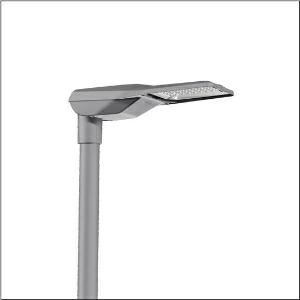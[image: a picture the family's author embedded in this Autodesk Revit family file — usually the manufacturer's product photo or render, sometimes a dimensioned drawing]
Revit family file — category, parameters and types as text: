
# Revit family: streetlight_sl_21_iq_mini___pl52_5xe2h31d08hb_f62b
name_source: partatom
category: Lighting Fixtures
units: mm (PartAtom-declared; Revit-internal decimal feet)

## family parameters
Cut with Voids When Loaded = No
Host = Face
Light Source = No
Part Type = Normal
Room Calculation Point = No
Round Connector Dimension = Use Diameter
Shared = No

## types (1)
- --- (1 x LED, 9290 lm, 70.9 W, 3000K)
    Apparent Load = 71 VA
    CIE Flux Codes = 27 59 98 100 100
    Color Rendering = 70
    Color Temperature = 3000K
    Default Elevation = 1800 mm
    Description = Streetlight SL 21 iQ mini, mast luminaire, primary light control with lens, of PMMA, primary optical cover: cover, of toughened safety glass, transparent, light distribution: PL52, light emission: direct distribution, primary light characteristic: asymmetric, installation type: post-top, side-entry, LED, High Power LED, rated luminous flux: 9.290lm, luminous efficacy: 131lm/W, light colour: 730, colour temperature: 3000K, control: Auto-Match, Temp-Guard, Lumen-Switch, Night-Set, Smart-Wire, Light-Fading, Desk-Remote (wireless, voltage-free reading and setting of iQ features in the workshop via application-optimized NFC function/RFID function), optimised constant luminous flux control (CLO 2.0), presetting dimming linear, mains connection: 220..240V, AC, 50/60Hz, start of lifetime: 71W, end of service life: 75W, reduction: 31W, luminaire housing, of diecast aluminium, powder-coated, Siteco® metallic grey (DB 702S), corrosivity category C5 mid according to DIN EN ISO 12944, please order mast flange separately, inclination adjustable: 0°, 5°, 10°, 15°, sealing non-destructively replaceable, multi-level sealing system, length: 628mm, width: 235mm, height: 110mm, mast flange for spigot size: 42mm (side-entry): 5XC10008XM4, 60/48mm (side-entry/post-top): 5XC10108XM2, 76/60mm (side-entry/post-top): 5XC10108XM1, protection rating (complete): IP66, insulation class (complete): insulation class II (safety insulation), certification: CE, ENEC, ENEC+, VDE, impact resistance: IK09, permissible operating ambient temperature for outdoor applications: -40..+50°C, standard-compliant lighting for roads and squares, packaging unit: 1 piece

Light Distribution: PL52
    Height = 110 mm
    Lamp = 1 x LED
    Lamp Light Flux = 9290 lm
    Lamp Power = 70.9 W
    Lamp count = 1
    Length = 625 mm
    Luminous efficacy = 131 lm/W
    Manufacturer = Siteco
    ModVariant = No
    Model = 5XE2H31D08HB
    Number of Poles = 1
    OnlyDefault = Yes
    Power Factor = 1
    Product Name = Streetlight SL 21 iQ mini | PL52
    Product group = mast luminaire | pylon top
    ProductGroupID = 6100
    Protection Class = Protection class II
    Protection Degree = IP 66
    RLX_Detail_Level = 1
    RLX_Emergency_Light_Flux = 0 lm
    RLX_Emergency_Type = 0
    RLX_Emergency_Type_DB = No
    RlxData = <blob elided: 101945 chars, md5=4c67f570>
    Socket = socket
    Standby Power = 0 W
    System Light Flux = 9290 lm
    System Power = 71 W
    Type Comments = factory setting: luminous flux: 100 % | dim-lin: 254 | 711 mA
    Type Image = l_1003519.jpg
    URL = http://relux.com
    VarID = @adj_090799
    Voltage = 0 V
    Weight = 0.00 kg
    Width = 234 mm

## geometry (parser evidence)
native form markers: Blend x4, Sweep x11
no freeform markers — native parametric forms only
